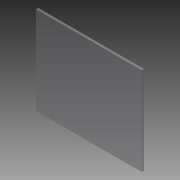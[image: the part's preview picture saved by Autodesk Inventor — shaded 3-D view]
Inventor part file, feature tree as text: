
AUTODESK INVENTOR PART (.ipt)
format: ipt  version: 2013 (Build 170138000, 138)  size: 68,096 bytes
history: native  units: in
note: dims shown in document units (in); Inventor stores cm internally (conversion verified against a paired STEP export)
features: extrude x1, sketch x1
ambient origin geometry x8: Origin, YZ Plane, XZ Plane, XY Plane, X Axis, Y Axis, Z Axis, Center Point
bodies: Solid1 (feature_tree)
feature tree (2):
  extrude  "Extrusion1"  Depth=6.0in
  sketch  "Sketch1"  dims[d0=5.0in d1=6.0in d2=0.125in d3=0.0in]
